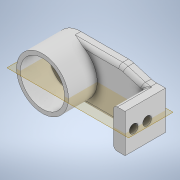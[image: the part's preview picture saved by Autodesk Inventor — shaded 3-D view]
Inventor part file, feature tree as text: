
AUTODESK INVENTOR PART (.ipt)
format: ipt  version: 2020 (Build 240168000, 168)  size: 234,496 bytes
history: native  units: in
note: dims shown in document units (in); Inventor stores cm internally (conversion verified against a paired STEP export)
features: fillet x6, extrude x5, sketch x5, mirror x1
ambient origin geometry x8: Origin, YZ Plane, XZ Plane, XY Plane, X Axis, Y Axis, Z Axis, Center Point
bodies: Solid1 (feature_tree)
feature tree (17):
  extrude  "Extrusion1"  Depth=0.9055in
  extrude  "Extrusion2"  Depth=0.1969in TaperAngle=0.0deg
  extrude  "Extrusion3"  Depth=0.1378in
  extrude  "Extrusion4"  Depth=0.1772in
  extrude  "Extrusion5"  Depth=0.2756in
  mirror  "Mirror1"
  fillet  "Fillet1"  Radius=2.0304in
  fillet  "Fillet2"  [1 undecoded]
  fillet  "Fillet3"  Radius=0.3937in
  fillet  "Fillet4"  Radius=0.3937in
  fillet  "Fillet5"  Radius=0.0787in
  fillet  "Fillet7"  Radius=0.0787in
  sketch  "Sketch1"  dims[d0=1.063in d1=0.9055in]
  sketch  "Sketch2"  dims[d2=0.5906in d3=0.0in d4=0.1969in d5=0.0in]
  sketch  "Sketch3"  dims[d6=0.7874in d7=0.1378in]
  sketch  "Sketch4"  dims[d8=0.2362in d9=0.0in d10=0.1772in]
  sketch  "Sketch5"  dims[d11=0.1772in d12=0.2756in d13=2.0304in d14=0.0in d15=0.0in d16=0.0in d17=0.3937in d18=0.3937in d19=0.0787in d20=0.0787in d21=0.0787in d23=0.0394in]
note: 1 required parameter value undecoded (feature->parameter linkage not recoverable at this tier; creation-order binding heuristic only, values carry confidence <= 0.55)
